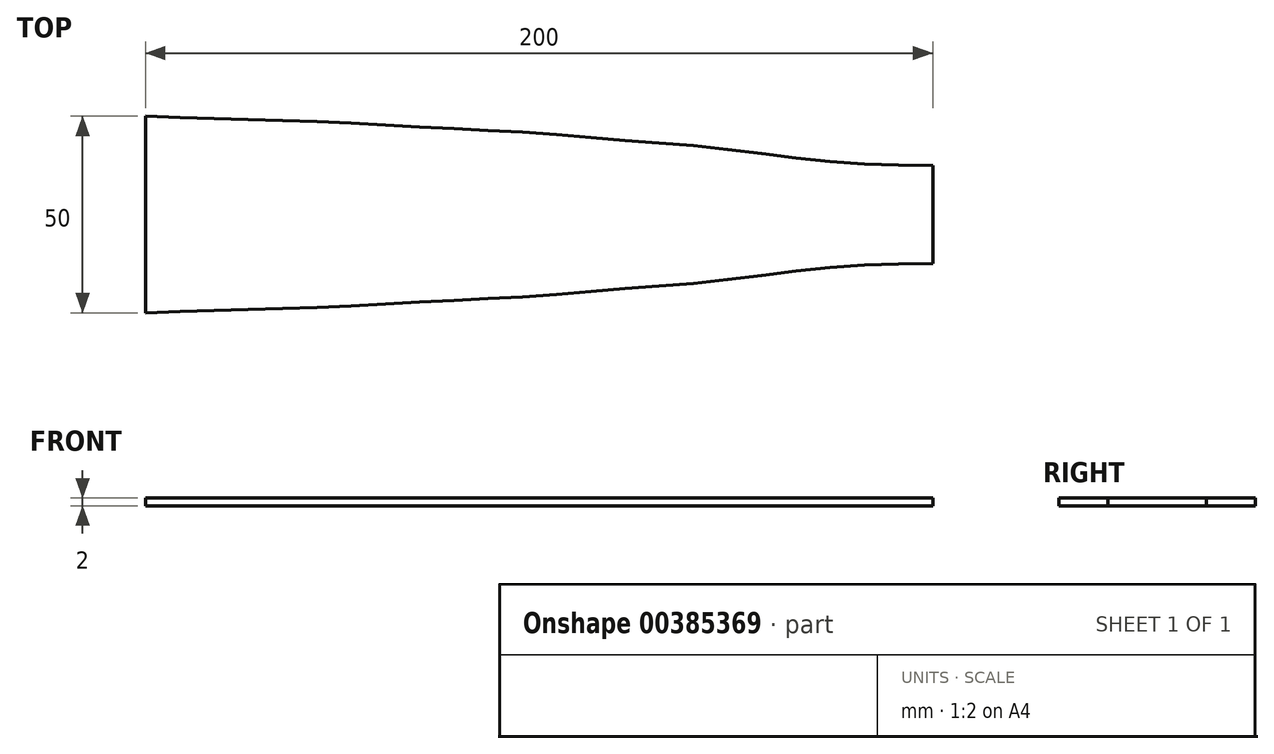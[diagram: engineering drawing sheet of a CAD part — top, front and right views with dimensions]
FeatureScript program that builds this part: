
annotation { "Feature Type Name" : "Feature", "Feature Type Description" : "" }
export const myFeature = defineFeature(function(context is Context, id is Id, definition is map)
    precondition{}
    {
        {
            var Q0;
            Q0=qCreatedBy(makeId("Top.planeOp"),FACE);
            var sketch = newSketch(context, id + "F0", { "sketchPlane" : qUnion([Q0])});
            skLineSegment(sketch, "E0", {"start": v(0, 25) * mm, "end": v(0, -25) * mm});
            skPoint(sketch, "E1", {"position": v(0, 0) * mm});
            skLineSegment(sketch, "E2", {"start": v(200, 12.5) * mm, "end": v(200, -12.5) * mm});
            skPoint(sketch, "E3", {"position": v(200, 0) * mm});
            skLineSegment(sketch, "E4", {"start": v(0, 0) * mm, "end": v(200, 0) * mm, "construction": true});
            skPoint(sketch, "E5", {"position": v(20, 24.3) * mm});
            skPoint(sketch, "E6", {"position": v(40, 23.7) * mm});
            skPoint(sketch, "E7", {"position": v(60, 22.8) * mm});
            skPoint(sketch, "E8", {"position": v(80, 21.7) * mm});
            skPoint(sketch, "E9", {"position": v(100, 20.7) * mm});
            skPoint(sketch, "E10", {"position": v(120, 19) * mm});
            skPoint(sketch, "E11", {"position": v(140, 17.4) * mm});
            skPoint(sketch, "E12", {"position": v(160, 15) * mm});
            skPoint(sketch, "E13", {"position": v(180, 13) * mm});
            skFitSpline(sketch, "E14", {"points": [v(0, 25) * mm, v(20, 24.3) * mm, v(40, 23.7) * mm, v(60, 22.8) * mm, v(80, 21.7) * mm, v(100, 20.7) * mm, v(120, 19) * mm, v(140, 17.4) * mm, v(160, 15) * mm, v(180, 13) * mm, v(200, 12.5) * mm], "startDerivative": vector(200.7, -7.36) * mm, "endDerivative": vector(200.27, -2.25) * mm});
            skFitSpline(sketch, "E15.MirrorCS", {"points": [v(0, -25) * mm, v(20, -24.3) * mm, v(40, -23.7) * mm, v(60, -22.8) * mm, v(80, -21.7) * mm, v(100, -20.7) * mm, v(120, -19) * mm, v(140, -17.4) * mm, v(160, -15) * mm, v(180, -13) * mm, v(200, -12.5) * mm], "startDerivative": vector(200.7, 7.36) * mm, "endDerivative": vector(200.27, 2.25) * mm});
            skSolve(sketch);
        }
        {
            var Q0;
            Q0=qSketchRegion(id+"F0",true);
            extrude(context, id + "F1", {"entities" : qUnion([Q0]), "depth" : 2 * mm});
        }
    });
